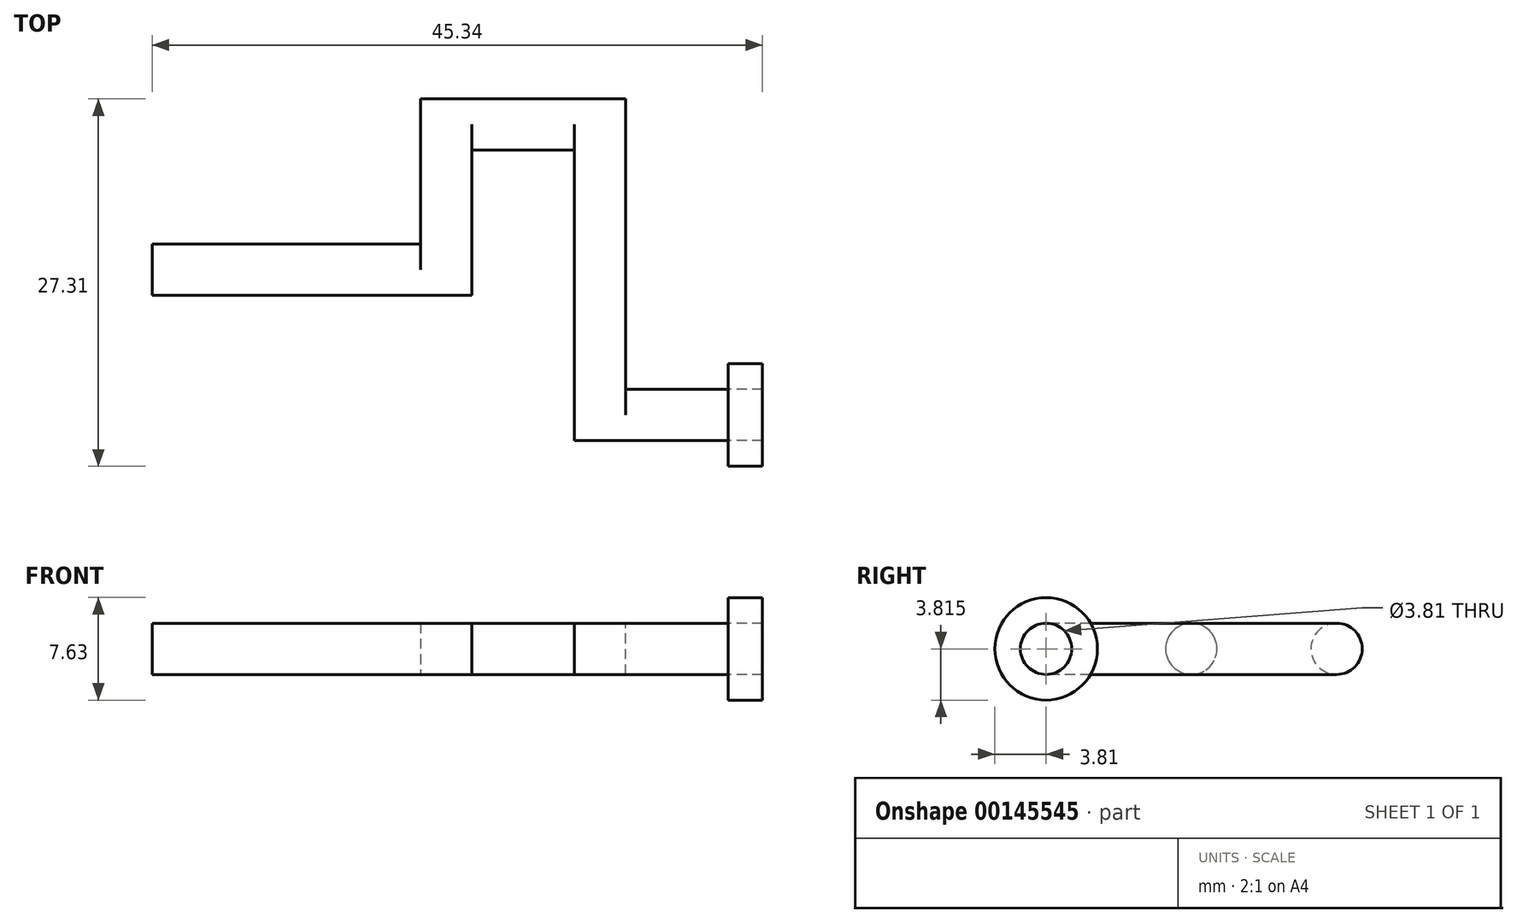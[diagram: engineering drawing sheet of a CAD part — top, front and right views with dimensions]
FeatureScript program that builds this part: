
annotation { "Feature Type Name" : "Feature", "Feature Type Description" : "" }
export const myFeature = defineFeature(function(context is Context, id is Id, definition is map)
    precondition{}
    {
        {
            var Q0;
            Q0=qCreatedBy(makeId("Top.planeOp"),FACE);
            var sketch = newSketch(context, id + "F0", { "sketchPlane" : qUnion([Q0])});
            skLineSegment(sketch, "E0", {"start": v(0, 0) * mm, "end": v(19.94, 0) * mm});
            skLineSegment(sketch, "E1", {"start": v(19.94, 0) * mm, "end": v(19.94, 10.8) * mm});
            skLineSegment(sketch, "E2", {"start": v(19.94, 10.8) * mm, "end": v(35.18, 10.8) * mm});
            skLineSegment(sketch, "E3", {"start": v(35.18, 10.8) * mm, "end": v(35.18, -10.8) * mm});
            skLineSegment(sketch, "E4", {"start": v(35.18, -10.8) * mm, "end": v(42.8, -10.8) * mm});
            skLineSegment(sketch, "E5", {"start": v(42.8, -10.8) * mm, "end": v(42.8, -14.6) * mm});
            skLineSegment(sketch, "E6", {"start": v(42.8, -14.6) * mm, "end": v(31.37, -14.6) * mm});
            skLineSegment(sketch, "E7", {"start": v(31.37, -14.6) * mm, "end": v(31.37, 6.99) * mm});
            skLineSegment(sketch, "E8", {"start": v(31.37, 6.99) * mm, "end": v(23.75, 6.99) * mm});
            skLineSegment(sketch, "E9", {"start": v(23.75, 6.99) * mm, "end": v(23.75, -3.8) * mm});
            skLineSegment(sketch, "E10", {"start": v(23.75, -3.8) * mm, "end": v(0, -3.81) * mm});
            skLineSegment(sketch, "E11", {"start": v(0, -3.81) * mm, "end": v(0, 0) * mm});
            skPoint(sketch, "E12", {"position": v(12.7, -3.81) * mm});
            skPoint(sketch, "E13", {"position": v(12.7, 0) * mm});
            skPoint(sketch, "E14", {"position": v(27.56, 6.99) * mm});
            skPoint(sketch, "E15", {"position": v(35.18, -1.9) * mm});
            skSolve(sketch);
        }
        {
            var Q0;
            Q0 = qSketchRegion(id + "F0", true);
            extrude(context, id + "F1", {"entities" : qUnion([Q0]), "depth" : 3.8 * mm});
        }
        {
            var Q0;
            Q0=makeQuery(id+"F1.opExtrude","CAP_EDGE",EDGE,{"disambiguationData":[OSD([sQuery(id+"F0.wireOp",EDGE,"E0")])],"isStart":false});
            var Q1;
            Q1=makeQuery(id+"F1.opExtrude","CAP_EDGE",EDGE,{"disambiguationData":[OSD([sQuery(id+"F0.wireOp",EDGE,"E0")])],"isStart":true});
            var Q2;
            Q2=makeQuery(id+"F1.opExtrude","CAP_EDGE",EDGE,{"disambiguationData":[OSD([sQuery(id+"F0.wireOp",EDGE,"E10")])],"isStart":false});
            var Q3;
            Q3=makeQuery(id+"F1.opExtrude","CAP_EDGE",EDGE,{"disambiguationData":[OSD([sQuery(id+"F0.wireOp",EDGE,"E10")])],"isStart":true});
            var Q4;
            Q4=makeQuery(id+"F1.opExtrude","CAP_EDGE",EDGE,{"disambiguationData":[OSD([sQuery(id+"F0.wireOp",EDGE,"E2")])],"isStart":false});
            var Q5;
            Q5=makeQuery(id+"F1.opExtrude","CAP_EDGE",EDGE,{"disambiguationData":[OSD([sQuery(id+"F0.wireOp",EDGE,"E8")])],"isStart":false});
            var Q6;
            Q6=makeQuery(id+"F1.opExtrude","CAP_EDGE",EDGE,{"disambiguationData":[OSD([sQuery(id+"F0.wireOp",EDGE,"E8")])],"isStart":true});
            var Q7;
            Q7=makeQuery(id+"F1.opExtrude","CAP_EDGE",EDGE,{"disambiguationData":[OSD([sQuery(id+"F0.wireOp",EDGE,"E2")])],"isStart":true});
            var Q8;
            Q8=makeQuery(id+"F1.opExtrude","CAP_EDGE",EDGE,{"disambiguationData":[OSD([sQuery(id+"F0.wireOp",EDGE,"E4")])],"isStart":false});
            var Q9;
            Q9=makeQuery(id+"F1.opExtrude","CAP_EDGE",EDGE,{"disambiguationData":[OSD([sQuery(id+"F0.wireOp",EDGE,"E6")])],"isStart":false});
            var Q10;
            Q10=makeQuery(id+"F1.opExtrude","CAP_EDGE",EDGE,{"disambiguationData":[OSD([sQuery(id+"F0.wireOp",EDGE,"E4")])],"isStart":true});
            var Q11;
            Q11=makeQuery(id+"F1.opExtrude","CAP_EDGE",EDGE,{"disambiguationData":[OSD([sQuery(id+"F0.wireOp",EDGE,"E6")])],"isStart":true});
            fillet(context, id + "F2", {"entities" : qUnion([Q0, Q1, Q2, Q3, Q4, Q5, Q6, Q7, Q8, Q9, Q10, Q11]), "radius" : 1.9 * mm, "tangentPropagation" : true, "allowEdgeOverflow" : false});
        }
        {
            var Q0;
            Q0=makeQuery(id+"F1.opExtrude","SWEPT_FACE",FACE,{"disambiguationData":[OSD([sQuery(id+"F0.wireOp",EDGE,"E5")])]});
            var sketch = newSketch(context, id + "F3", { "sketchPlane" : qUnion([Q0])});
            skCircle(sketch, "E16", {"center": v(-12.7, 1.9) * mm, "radius": 3.81 * mm});
            skSolve(sketch);
        }
        {
            var Q0;
            Q0=makeQuery(id+"F3.imprint","IMPRINT",FACE,{"disambiguationData":[TD([[makeQuery(id+"F3.imprint","IMPRINT",EDGE,{"derivedFrom":sQuery(id+"F3.wireOp",EDGE,"E16")}),1.0]])]});
            var Q1;
            Q1=makeQuery(id+"F3.imprint","IMPRINT",FACE,{"disambiguationData":[TD([[makeQuery(id+"F3.imprint","IMPRINT",EDGE,{"derivedFrom":makeQuery(id+"F2.opFillet","BLEND_EDGE",EDGE,{"blendedFrom":[makeQuery(id+"F1.opExtrude","CAP_EDGE",EDGE,{"disambiguationData":[OSD([sQuery(id+"F0.wireOp",EDGE,"E6")])],"isStart":false}),makeQuery(id+"F1.opExtrude","SWEPT_FACE",FACE,{"disambiguationData":[OSD([sQuery(id+"F0.wireOp",EDGE,"E5")])]})],"blendedInto":[makeQuery(id+"F1.opExtrude","SWEPT_FACE",FACE,{"disambiguationData":[OSD([sQuery(id+"F0.wireOp",EDGE,"E5")])]})]})}),1.0]])]});
            extrude(context, id + "F4", {"entities" : qUnion([Q0, Q1]), "operationType" : NewBodyOperationType.ADD, "depth" : 2.54 * mm});
        }
    });
